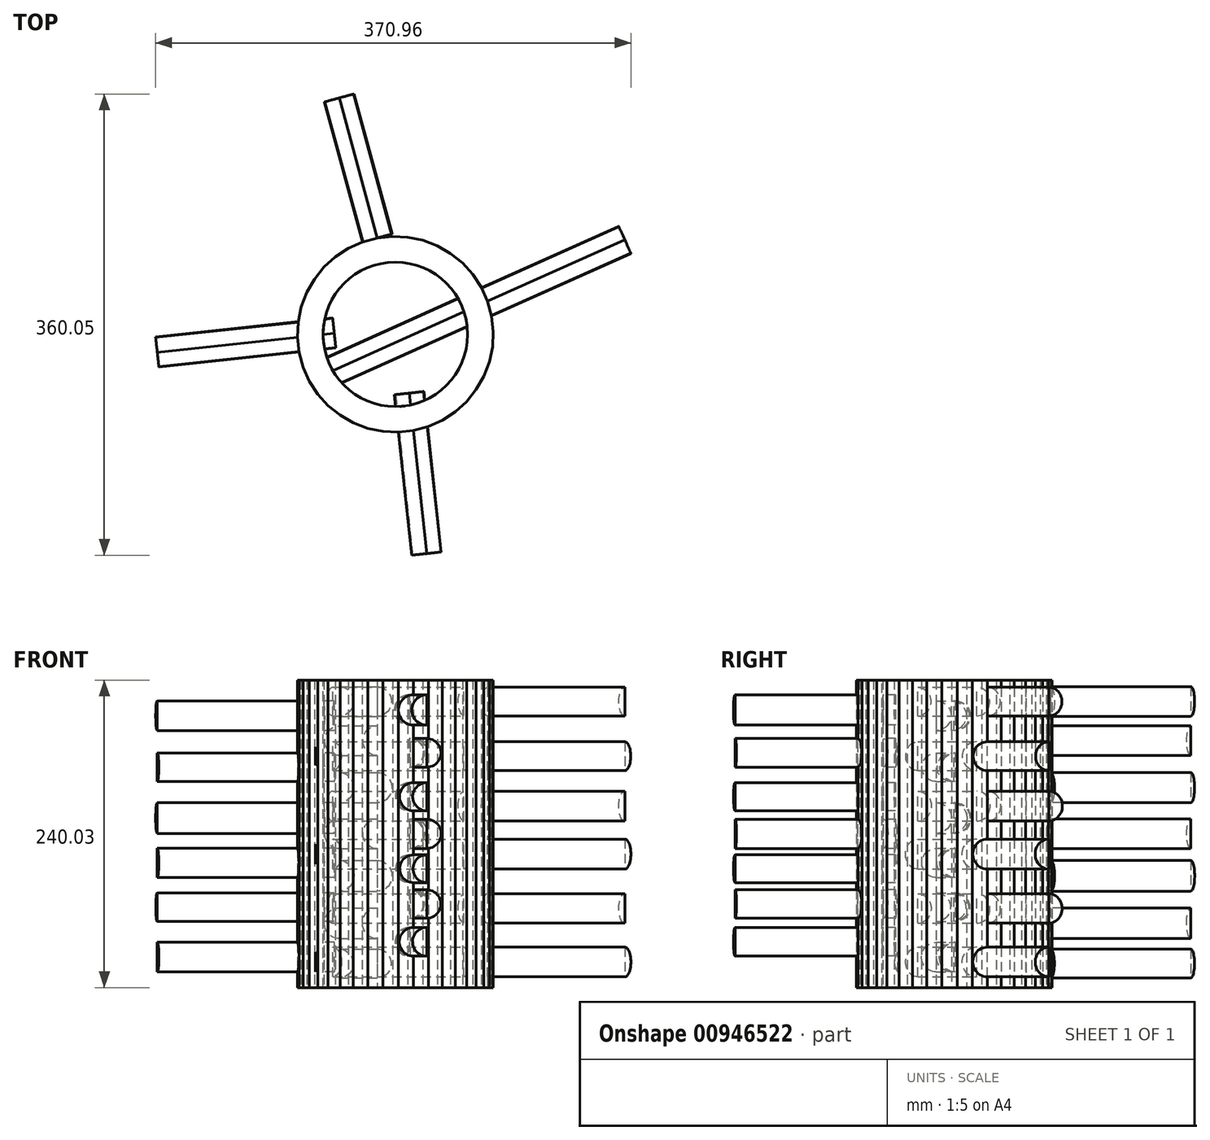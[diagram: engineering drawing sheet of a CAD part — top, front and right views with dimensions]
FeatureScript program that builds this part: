
annotation { "Feature Type Name" : "Feature", "Feature Type Description" : "" }
export const myFeature = defineFeature(function(context is Context, id is Id, definition is map)
    precondition{}
    {
        {
            var Q0;
            Q0=qCreatedBy(makeId("Top.planeOp"),FACE);
            var sketch = newSketch(context, id + "F0", { "sketchPlane" : qUnion([Q0])});
            skCircle(sketch, "E0.cCircle", {"center": v(0, 0) * mm, "radius": 76.25 * mm, "construction": true});
            skLineSegment(sketch, "E0.0", {"start": v(69.13, -32.73) * mm, "end": v(63.16, -43.14) * mm});
            skLineSegment(sketch, "E0.1", {"start": v(63.16, -43.14) * mm, "end": v(55.64, -52.5) * mm});
            skLineSegment(sketch, "E0.2", {"start": v(55.64, -52.5) * mm, "end": v(46.74, -60.55) * mm});
            skLineSegment(sketch, "E0.3", {"start": v(46.74, -60.55) * mm, "end": v(36.7, -67.11) * mm});
            skLineSegment(sketch, "E0.4", {"start": v(36.7, -67.11) * mm, "end": v(25.74, -72.03) * mm});
            skLineSegment(sketch, "E0.5", {"start": v(25.74, -72.03) * mm, "end": v(14.16, -75.17) * mm});
            skLineSegment(sketch, "E0.6", {"start": v(14.16, -75.17) * mm, "end": v(2.22, -76.46) * mm});
            skLineSegment(sketch, "E0.7", {"start": v(2.22, -76.46) * mm, "end": v(-9.76, -75.86) * mm});
            skLineSegment(sketch, "E0.8", {"start": v(-9.76, -75.86) * mm, "end": v(-21.51, -73.4) * mm});
            skLineSegment(sketch, "E0.9", {"start": v(-21.51, -73.4) * mm, "end": v(-32.73, -69.13) * mm});
            skLineSegment(sketch, "E0.10", {"start": v(-32.73, -69.13) * mm, "end": v(-43.14, -63.16) * mm});
            skLineSegment(sketch, "E0.11", {"start": v(-43.14, -63.16) * mm, "end": v(-52.5, -55.64) * mm});
            skLineSegment(sketch, "E0.12", {"start": v(-52.5, -55.64) * mm, "end": v(-60.55, -46.74) * mm});
            skLineSegment(sketch, "E0.13", {"start": v(-60.55, -46.74) * mm, "end": v(-67.11, -36.7) * mm});
            skLineSegment(sketch, "E0.14", {"start": v(-67.11, -36.7) * mm, "end": v(-72.03, -25.74) * mm});
            skLineSegment(sketch, "E0.15", {"start": v(-72.03, -25.74) * mm, "end": v(-75.17, -14.16) * mm});
            skLineSegment(sketch, "E0.16", {"start": v(-75.17, -14.16) * mm, "end": v(-76.46, -2.22) * mm});
            skLineSegment(sketch, "E0.17", {"start": v(-76.46, -2.22) * mm, "end": v(-75.86, 9.76) * mm});
            skLineSegment(sketch, "E0.18", {"start": v(-75.86, 9.76) * mm, "end": v(-73.4, 21.51) * mm});
            skLineSegment(sketch, "E0.19", {"start": v(-73.4, 21.51) * mm, "end": v(-69.13, 32.73) * mm});
            skLineSegment(sketch, "E0.20", {"start": v(-69.13, 32.73) * mm, "end": v(-63.16, 43.14) * mm});
            skLineSegment(sketch, "E0.21", {"start": v(-63.16, 43.14) * mm, "end": v(-55.64, 52.5) * mm});
            skLineSegment(sketch, "E0.22", {"start": v(-55.64, 52.5) * mm, "end": v(-46.74, 60.55) * mm});
            skLineSegment(sketch, "E0.23", {"start": v(-46.74, 60.55) * mm, "end": v(-36.7, 67.11) * mm});
            skLineSegment(sketch, "E0.24", {"start": v(-36.7, 67.11) * mm, "end": v(-25.74, 72.03) * mm});
            skLineSegment(sketch, "E0.25", {"start": v(-25.74, 72.03) * mm, "end": v(-14.16, 75.17) * mm});
            skLineSegment(sketch, "E0.26", {"start": v(-14.16, 75.17) * mm, "end": v(-2.22, 76.46) * mm});
            skLineSegment(sketch, "E0.27", {"start": v(-2.22, 76.46) * mm, "end": v(9.76, 75.86) * mm});
            skLineSegment(sketch, "E0.28", {"start": v(9.76, 75.86) * mm, "end": v(21.51, 73.4) * mm});
            skLineSegment(sketch, "E0.29", {"start": v(21.51, 73.4) * mm, "end": v(32.73, 69.13) * mm});
            skLineSegment(sketch, "E0.30", {"start": v(32.73, 69.13) * mm, "end": v(43.14, 63.16) * mm});
            skLineSegment(sketch, "E0.31", {"start": v(43.14, 63.16) * mm, "end": v(52.5, 55.64) * mm});
            skLineSegment(sketch, "E0.32", {"start": v(52.5, 55.64) * mm, "end": v(60.55, 46.74) * mm});
            skLineSegment(sketch, "E0.33", {"start": v(60.55, 46.74) * mm, "end": v(67.11, 36.7) * mm});
            skLineSegment(sketch, "E0.34", {"start": v(67.11, 36.7) * mm, "end": v(72.03, 25.74) * mm});
            skLineSegment(sketch, "E0.35", {"start": v(72.03, 25.74) * mm, "end": v(75.17, 14.16) * mm});
            skLineSegment(sketch, "E0.36", {"start": v(75.17, 14.16) * mm, "end": v(76.46, 2.22) * mm});
            skLineSegment(sketch, "E0.37", {"start": v(76.46, 2.22) * mm, "end": v(75.86, -9.76) * mm});
            skLineSegment(sketch, "E0.38", {"start": v(75.86, -9.76) * mm, "end": v(73.4, -21.51) * mm});
            skLineSegment(sketch, "E0.39", {"start": v(73.4, -21.51) * mm, "end": v(69.13, -32.73) * mm});
            skPoint(sketch, "E0.0.midPoint", {"position": v(66.15, -37.94) * mm});
            skSolve(sketch);
        }
        {
            var Q0;
            Q0=makeQuery(id+"F0.imprint","IMPRINT",FACE,{"disambiguationData":[TD([[makeQuery(id+"F0.imprint","IMPRINT",EDGE,{"derivedFrom":sQuery(id+"F0.wireOp",EDGE,"E0.0")}),-1.0]])]});
            extrude(context, id + "F1", {"entities" : qUnion([Q0]), "depth" : 240.03 * mm, "offsetDistance" : 25.4 * mm});
        }
        {
            var Q0;
            Q0=makeQuery(id+"F1.opExtrude","CAP_FACE",FACE,{"disambiguationData":[OSD([sQuery(id+"F0.wireOp",EDGE,"E0.0"),sQuery(id+"F0.wireOp",EDGE,"E0.1"),sQuery(id+"F0.wireOp",EDGE,"E0.2"),sQuery(id+"F0.wireOp",EDGE,"E0.3"),sQuery(id+"F0.wireOp",EDGE,"E0.4"),sQuery(id+"F0.wireOp",EDGE,"E0.5"),sQuery(id+"F0.wireOp",EDGE,"E0.6"),sQuery(id+"F0.wireOp",EDGE,"E0.7"),sQuery(id+"F0.wireOp",EDGE,"E0.8"),sQuery(id+"F0.wireOp",EDGE,"E0.9"),sQuery(id+"F0.wireOp",EDGE,"E0.10"),sQuery(id+"F0.wireOp",EDGE,"E0.11"),sQuery(id+"F0.wireOp",EDGE,"E0.12"),sQuery(id+"F0.wireOp",EDGE,"E0.13"),sQuery(id+"F0.wireOp",EDGE,"E0.14"),sQuery(id+"F0.wireOp",EDGE,"E0.15"),sQuery(id+"F0.wireOp",EDGE,"E0.16"),sQuery(id+"F0.wireOp",EDGE,"E0.17"),sQuery(id+"F0.wireOp",EDGE,"E0.18"),sQuery(id+"F0.wireOp",EDGE,"E0.19"),sQuery(id+"F0.wireOp",EDGE,"E0.20"),sQuery(id+"F0.wireOp",EDGE,"E0.21"),sQuery(id+"F0.wireOp",EDGE,"E0.22"),sQuery(id+"F0.wireOp",EDGE,"E0.23"),sQuery(id+"F0.wireOp",EDGE,"E0.24"),sQuery(id+"F0.wireOp",EDGE,"E0.25"),sQuery(id+"F0.wireOp",EDGE,"E0.26"),sQuery(id+"F0.wireOp",EDGE,"E0.27"),sQuery(id+"F0.wireOp",EDGE,"E0.28"),sQuery(id+"F0.wireOp",EDGE,"E0.29"),sQuery(id+"F0.wireOp",EDGE,"E0.30"),sQuery(id+"F0.wireOp",EDGE,"E0.31"),sQuery(id+"F0.wireOp",EDGE,"E0.32"),sQuery(id+"F0.wireOp",EDGE,"E0.33"),sQuery(id+"F0.wireOp",EDGE,"E0.34"),sQuery(id+"F0.wireOp",EDGE,"E0.35"),sQuery(id+"F0.wireOp",EDGE,"E0.36"),sQuery(id+"F0.wireOp",EDGE,"E0.37"),sQuery(id+"F0.wireOp",EDGE,"E0.38"),sQuery(id+"F0.wireOp",EDGE,"E0.39")])],"isStart":false});
            var sketch = newSketch(context, id + "F2", { "sketchPlane" : qUnion([Q0])});
            skCircle(sketch, "E1", {"center": v(0, 0) * mm, "radius": 56.38 * mm});
            skSolve(sketch);
        }
        {
            var Q0;
            Q0=makeQuery(id+"F2.imprint","IMPRINT",FACE,{"disambiguationData":[TD([[makeQuery(id+"F2.imprint","IMPRINT",EDGE,{"derivedFrom":sQuery(id+"F2.wireOp",EDGE,"E1")}),1.0]])]});
            extrude(context, id + "F3", {"entities" : qUnion([Q0]), "operationType" : NewBodyOperationType.REMOVE, "oppositeDirection" : true, "depth" : 425.96 * mm, "offsetDistance" : 25.4 * mm});
        }
        {
            var Q0;
            Q0=makeQuery(id+"F1.opExtrude","SWEPT_FACE",FACE,{"disambiguationData":[OSD([sQuery(id+"F0.wireOp",EDGE,"E0.6")])]});
            var sketch = newSketch(context, id + "F4", { "sketchPlane" : qUnion([Q0])});
            skCircle(sketch, "E2", {"center": v(6, 183.22) * mm, "radius": 11.15 * mm});
            skCircle(sketch, "E3", {"center": v(6, 149) * mm, "radius": 11.02 * mm});
            skPoint(sketch, "E4.center.orphan", {"position": v(6, 120.02) * mm});
            skCircle(sketch, "E5", {"center": v(6, 120.02) * mm, "radius": 11.4 * mm});
            skCircle(sketch, "E6", {"center": v(6, 92.73) * mm, "radius": 10.84 * mm});
            skCircle(sketch, "E7", {"center": v(6, 65.2) * mm, "radius": 11.04 * mm});
            skCircle(sketch, "E8", {"center": v(6, 35.69) * mm, "radius": 11.2 * mm});
            skCircle(sketch, "E9", {"center": v(6, 216.66) * mm, "radius": 11.8 * mm});
            skSolve(sketch);
        }
        {
            var Q0;
            {var subQ0=sQuery(id+"F4.wireOp",EDGE,"E9");var subQ1=makeQuery(id+"F1.opExtrude","SWEPT_EDGE",EDGE,{"disambiguationData":[OSD([sQuery(id+"F0.wireOp",EDGE,"E0.5"),sQuery(id+"F0.wireOp",EDGE,"E0.6")])]});var subQ2=makeQuery(id+"F4.imprint","INTERSECT",VERTEX,{"disambiguationData":[OD(0.0)],"derivedFrom":[subQ1,subQ0]});Q0=makeQuery(id+"F4.imprint","IMPRINT",FACE,{"disambiguationData":[TD([[makeQuery(id+"F4.imprint","IMPRINT",EDGE,{"disambiguationData":[TD([[subQ2,-1.0]])],"derivedFrom":subQ0}),1.0]])]});}
            var Q1;
            {var subQ0=sQuery(id+"F4.wireOp",EDGE,"E2");var subQ1=makeQuery(id+"F1.opExtrude","SWEPT_EDGE",EDGE,{"disambiguationData":[OSD([sQuery(id+"F0.wireOp",EDGE,"E0.5"),sQuery(id+"F0.wireOp",EDGE,"E0.6")])]});var subQ2=makeQuery(id+"F4.imprint","INTERSECT",VERTEX,{"disambiguationData":[OD(0.0)],"derivedFrom":[subQ1,subQ0]});Q1=makeQuery(id+"F4.imprint","IMPRINT",FACE,{"disambiguationData":[TD([[makeQuery(id+"F4.imprint","IMPRINT",EDGE,{"disambiguationData":[TD([[subQ2,1.0]])],"derivedFrom":subQ0}),1.0]])]});}
            var Q2;
            {var subQ0=sQuery(id+"F4.wireOp",EDGE,"E3");var subQ1=makeQuery(id+"F1.opExtrude","SWEPT_EDGE",EDGE,{"disambiguationData":[OSD([sQuery(id+"F0.wireOp",EDGE,"E0.5"),sQuery(id+"F0.wireOp",EDGE,"E0.6")])]});var subQ2=makeQuery(id+"F4.imprint","INTERSECT",VERTEX,{"disambiguationData":[OD(0.0)],"derivedFrom":[subQ1,subQ0]});Q2=makeQuery(id+"F4.imprint","IMPRINT",FACE,{"disambiguationData":[TD([[makeQuery(id+"F4.imprint","IMPRINT",EDGE,{"disambiguationData":[TD([[subQ2,-1.0]])],"derivedFrom":subQ0}),1.0]])]});}
            var Q3;
            {var subQ0=sQuery(id+"F4.wireOp",EDGE,"E5");var subQ1=makeQuery(id+"F1.opExtrude","SWEPT_EDGE",EDGE,{"disambiguationData":[OSD([sQuery(id+"F0.wireOp",EDGE,"E0.5"),sQuery(id+"F0.wireOp",EDGE,"E0.6")])]});var subQ2=makeQuery(id+"F4.imprint","INTERSECT",VERTEX,{"disambiguationData":[OD(0.0)],"derivedFrom":[subQ1,subQ0]});Q3=makeQuery(id+"F4.imprint","IMPRINT",FACE,{"disambiguationData":[TD([[makeQuery(id+"F4.imprint","IMPRINT",EDGE,{"disambiguationData":[TD([[subQ2,1.0]])],"derivedFrom":subQ0}),1.0]])]});}
            var Q4;
            {var subQ0=sQuery(id+"F4.wireOp",EDGE,"E6");var subQ1=makeQuery(id+"F1.opExtrude","SWEPT_EDGE",EDGE,{"disambiguationData":[OSD([sQuery(id+"F0.wireOp",EDGE,"E0.5"),sQuery(id+"F0.wireOp",EDGE,"E0.6")])]});var subQ2=makeQuery(id+"F4.imprint","INTERSECT",VERTEX,{"disambiguationData":[OD(0.0)],"derivedFrom":[subQ1,subQ0]});Q4=makeQuery(id+"F4.imprint","IMPRINT",FACE,{"disambiguationData":[TD([[makeQuery(id+"F4.imprint","IMPRINT",EDGE,{"disambiguationData":[TD([[subQ2,1.0]])],"derivedFrom":subQ0}),1.0]])]});}
            var Q5;
            {var subQ0=sQuery(id+"F4.wireOp",EDGE,"E7");var subQ1=makeQuery(id+"F1.opExtrude","SWEPT_EDGE",EDGE,{"disambiguationData":[OSD([sQuery(id+"F0.wireOp",EDGE,"E0.5"),sQuery(id+"F0.wireOp",EDGE,"E0.6")])]});var subQ2=makeQuery(id+"F4.imprint","INTERSECT",VERTEX,{"disambiguationData":[OD(0.0)],"derivedFrom":[subQ1,subQ0]});Q5=makeQuery(id+"F4.imprint","IMPRINT",FACE,{"disambiguationData":[TD([[makeQuery(id+"F4.imprint","IMPRINT",EDGE,{"disambiguationData":[TD([[subQ2,-1.0]])],"derivedFrom":subQ0}),1.0]])]});}
            var Q6;
            {var subQ0=sQuery(id+"F4.wireOp",EDGE,"E8");var subQ1=makeQuery(id+"F1.opExtrude","SWEPT_EDGE",EDGE,{"disambiguationData":[OSD([sQuery(id+"F0.wireOp",EDGE,"E0.5"),sQuery(id+"F0.wireOp",EDGE,"E0.6")])]});var subQ2=makeQuery(id+"F4.imprint","INTERSECT",VERTEX,{"disambiguationData":[OD(0.0)],"derivedFrom":[subQ1,subQ0]});Q6=makeQuery(id+"F4.imprint","IMPRINT",FACE,{"disambiguationData":[TD([[makeQuery(id+"F4.imprint","IMPRINT",EDGE,{"disambiguationData":[TD([[subQ2,1.0]])],"derivedFrom":subQ0}),1.0]])]});}
            extrude(context, id + "F5", {"entities" : qUnion([Q0, Q1, Q2, Q3, Q4, Q5, Q6]), "operationType" : NewBodyOperationType.ADD, "oppositeDirection" : true, "depth" : 29.46 * mm, "offsetDistance" : 25.4 * mm});
        }
        {
            var Q0;
            Q0=makeQuery(id+"F5.opExtrude","CAP_FACE",FACE,{"disambiguationData":[OSD([sQuery(id+"F0.wireOp",EDGE,"E0.5"),sQuery(id+"F0.wireOp",EDGE,"E0.6"),sQuery(id+"F4.wireOp",EDGE,"E9")])],"isStart":false});
            var Q1;
            Q1=makeQuery(id+"F5.opExtrude","CAP_FACE",FACE,{"disambiguationData":[OSD([sQuery(id+"F0.wireOp",EDGE,"E0.5"),sQuery(id+"F0.wireOp",EDGE,"E0.6"),sQuery(id+"F4.wireOp",EDGE,"E2")])],"isStart":false});
            var Q2;
            Q2=makeQuery(id+"F5.opExtrude","CAP_FACE",FACE,{"disambiguationData":[OSD([sQuery(id+"F0.wireOp",EDGE,"E0.5"),sQuery(id+"F0.wireOp",EDGE,"E0.6"),sQuery(id+"F4.wireOp",EDGE,"E3")])],"isStart":false});
            var Q3;
            Q3=makeQuery(id+"F5.opExtrude","CAP_FACE",FACE,{"disambiguationData":[OSD([sQuery(id+"F0.wireOp",EDGE,"E0.5"),sQuery(id+"F0.wireOp",EDGE,"E0.6"),sQuery(id+"F4.wireOp",EDGE,"E5")])],"isStart":false});
            var Q4;
            Q4=makeQuery(id+"F5.opExtrude","CAP_FACE",FACE,{"disambiguationData":[OSD([sQuery(id+"F0.wireOp",EDGE,"E0.5"),sQuery(id+"F0.wireOp",EDGE,"E0.6"),sQuery(id+"F4.wireOp",EDGE,"E6")])],"isStart":false});
            var Q5;
            Q5=makeQuery(id+"F5.opExtrude","CAP_FACE",FACE,{"disambiguationData":[OSD([sQuery(id+"F0.wireOp",EDGE,"E0.5"),sQuery(id+"F0.wireOp",EDGE,"E0.6"),sQuery(id+"F4.wireOp",EDGE,"E8")])],"isStart":false});
            var Q6;
            Q6=makeQuery(id+"F5.opExtrude","CAP_FACE",FACE,{"disambiguationData":[OSD([sQuery(id+"F0.wireOp",EDGE,"E0.5"),sQuery(id+"F0.wireOp",EDGE,"E0.6"),sQuery(id+"F4.wireOp",EDGE,"E7")])],"isStart":false});
            extrude(context, id + "F6", {"entities" : qUnion([Q0, Q1, Q2, Q3, Q4, Q5, Q6]), "operationType" : NewBodyOperationType.ADD, "oppositeDirection" : true, "depth" : 125.98 * mm, "offsetDistance" : 25.4 * mm});
        }
        {
            var Q0;
            Q0=makeQuery(id+"F1.opExtrude","SWEPT_FACE",FACE,{"disambiguationData":[OSD([sQuery(id+"F0.wireOp",EDGE,"E0.25")])]});
            var sketch = newSketch(context, id + "F7", { "sketchPlane" : qUnion([Q0])});
            skCircle(sketch, "E10", {"center": v(-6, 223.35) * mm, "radius": 11.6 * mm});
            skCircle(sketch, "E11", {"center": v(-6, 192.66) * mm, "radius": 11.6 * mm});
            skCircle(sketch, "E12", {"center": v(-6, 156.07) * mm, "radius": 11.78 * mm});
            skCircle(sketch, "E13", {"center": v(-6, 120.02) * mm, "radius": 11.63 * mm});
            skCircle(sketch, "E14", {"center": v(-6, 87.23) * mm, "radius": 12.03 * mm});
            skCircle(sketch, "E15", {"center": v(-6, 50.25) * mm, "radius": 11.97 * mm});
            skCircle(sketch, "E16", {"center": v(-6, 18.77) * mm, "radius": 11.25 * mm});
            skSolve(sketch);
        }
        {
            var Q0;
            {var subQ0=sQuery(id+"F7.wireOp",EDGE,"E10");var subQ1=makeQuery(id+"F1.opExtrude","SWEPT_EDGE",EDGE,{"disambiguationData":[OSD([sQuery(id+"F0.wireOp",EDGE,"E0.25"),sQuery(id+"F0.wireOp",EDGE,"E0.26")])]});var subQ2=makeQuery(id+"F7.imprint","INTERSECT",VERTEX,{"disambiguationData":[OD(0.0)],"derivedFrom":[subQ1,subQ0]});Q0=makeQuery(id+"F7.imprint","IMPRINT",FACE,{"disambiguationData":[TD([[makeQuery(id+"F7.imprint","IMPRINT",EDGE,{"disambiguationData":[TD([[subQ2,-1.0]])],"derivedFrom":subQ0}),1.0]])]});}
            var Q1;
            {var subQ0=sQuery(id+"F7.wireOp",EDGE,"E11");var subQ1=makeQuery(id+"F1.opExtrude","SWEPT_EDGE",EDGE,{"disambiguationData":[OSD([sQuery(id+"F0.wireOp",EDGE,"E0.25"),sQuery(id+"F0.wireOp",EDGE,"E0.26")])]});var subQ2=makeQuery(id+"F7.imprint","INTERSECT",VERTEX,{"disambiguationData":[OD(0.0)],"derivedFrom":[subQ1,subQ0]});Q1=makeQuery(id+"F7.imprint","IMPRINT",FACE,{"disambiguationData":[TD([[makeQuery(id+"F7.imprint","IMPRINT",EDGE,{"disambiguationData":[TD([[subQ2,1.0]])],"derivedFrom":subQ0}),1.0]])]});}
            var Q2;
            {var subQ0=sQuery(id+"F7.wireOp",EDGE,"E12");var subQ1=makeQuery(id+"F1.opExtrude","SWEPT_EDGE",EDGE,{"disambiguationData":[OSD([sQuery(id+"F0.wireOp",EDGE,"E0.25"),sQuery(id+"F0.wireOp",EDGE,"E0.26")])]});var subQ2=makeQuery(id+"F7.imprint","INTERSECT",VERTEX,{"disambiguationData":[OD(0.0)],"derivedFrom":[subQ1,subQ0]});Q2=makeQuery(id+"F7.imprint","IMPRINT",FACE,{"disambiguationData":[TD([[makeQuery(id+"F7.imprint","IMPRINT",EDGE,{"disambiguationData":[TD([[subQ2,1.0]])],"derivedFrom":subQ0}),1.0]])]});}
            var Q3;
            {var subQ0=sQuery(id+"F7.wireOp",EDGE,"E13");var subQ1=makeQuery(id+"F1.opExtrude","SWEPT_EDGE",EDGE,{"disambiguationData":[OSD([sQuery(id+"F0.wireOp",EDGE,"E0.25"),sQuery(id+"F0.wireOp",EDGE,"E0.26")])]});var subQ2=makeQuery(id+"F7.imprint","INTERSECT",VERTEX,{"disambiguationData":[OD(0.0)],"derivedFrom":[subQ1,subQ0]});Q3=makeQuery(id+"F7.imprint","IMPRINT",FACE,{"disambiguationData":[TD([[makeQuery(id+"F7.imprint","IMPRINT",EDGE,{"disambiguationData":[TD([[subQ2,-1.0]])],"derivedFrom":subQ0}),1.0]])]});}
            var Q4;
            {var subQ0=sQuery(id+"F7.wireOp",EDGE,"E14");var subQ1=makeQuery(id+"F1.opExtrude","SWEPT_EDGE",EDGE,{"disambiguationData":[OSD([sQuery(id+"F0.wireOp",EDGE,"E0.25"),sQuery(id+"F0.wireOp",EDGE,"E0.26")])]});var subQ2=makeQuery(id+"F7.imprint","INTERSECT",VERTEX,{"disambiguationData":[OD(0.0)],"derivedFrom":[subQ1,subQ0]});Q4=makeQuery(id+"F7.imprint","IMPRINT",FACE,{"disambiguationData":[TD([[makeQuery(id+"F7.imprint","IMPRINT",EDGE,{"disambiguationData":[TD([[subQ2,-1.0]])],"derivedFrom":subQ0}),1.0]])]});}
            var Q5;
            {var subQ0=sQuery(id+"F7.wireOp",EDGE,"E15");var subQ1=makeQuery(id+"F1.opExtrude","SWEPT_EDGE",EDGE,{"disambiguationData":[OSD([sQuery(id+"F0.wireOp",EDGE,"E0.25"),sQuery(id+"F0.wireOp",EDGE,"E0.26")])]});var subQ2=makeQuery(id+"F7.imprint","INTERSECT",VERTEX,{"disambiguationData":[OD(0.0)],"derivedFrom":[subQ1,subQ0]});Q5=makeQuery(id+"F7.imprint","IMPRINT",FACE,{"disambiguationData":[TD([[makeQuery(id+"F7.imprint","IMPRINT",EDGE,{"disambiguationData":[TD([[subQ2,1.0]])],"derivedFrom":subQ0}),1.0]])]});}
            var Q6;
            {var subQ0=sQuery(id+"F7.wireOp",EDGE,"E16");var subQ1=makeQuery(id+"F1.opExtrude","SWEPT_EDGE",EDGE,{"disambiguationData":[OSD([sQuery(id+"F0.wireOp",EDGE,"E0.25"),sQuery(id+"F0.wireOp",EDGE,"E0.26")])]});var subQ2=makeQuery(id+"F7.imprint","INTERSECT",VERTEX,{"disambiguationData":[OD(0.0)],"derivedFrom":[subQ1,subQ0]});Q6=makeQuery(id+"F7.imprint","IMPRINT",FACE,{"disambiguationData":[TD([[makeQuery(id+"F7.imprint","IMPRINT",EDGE,{"disambiguationData":[TD([[subQ2,1.0]])],"derivedFrom":subQ0}),1.0]])]});}
            extrude(context, id + "F8", {"entities" : qUnion([Q0, Q1, Q2, Q3, Q4, Q5, Q6]), "operationType" : NewBodyOperationType.ADD, "depth" : 113.28 * mm, "offsetDistance" : 25.4 * mm});
        }
        {
            var Q0;
            Q0=makeQuery(id+"F1.opExtrude","SWEPT_FACE",FACE,{"disambiguationData":[OSD([sQuery(id+"F0.wireOp",EDGE,"E0.16")])]});
            var sketch = newSketch(context, id + "F9", { "sketchPlane" : qUnion([Q0])});
            skCircle(sketch, "E17", {"center": v(-6, 23.76) * mm, "radius": 11.6 * mm});
            skCircle(sketch, "E18", {"center": v(-6, 62.71) * mm, "radius": 11.2 * mm});
            skCircle(sketch, "E19", {"center": v(-6, 97.29) * mm, "radius": 11.37 * mm});
            skCircle(sketch, "E20", {"center": v(-6, 132.3) * mm, "radius": 11.97 * mm});
            skCircle(sketch, "E21", {"center": v(-6, 171.94) * mm, "radius": 11.22 * mm});
            skCircle(sketch, "E22", {"center": v(-6, 212.2) * mm, "radius": 11.6 * mm});
            skSolve(sketch);
        }
        {
            var Q0;
            {var subQ0=sQuery(id+"F9.wireOp",EDGE,"E17");var subQ1=makeQuery(id+"F1.opExtrude","SWEPT_EDGE",EDGE,{"disambiguationData":[OSD([sQuery(id+"F0.wireOp",EDGE,"E0.16"),sQuery(id+"F0.wireOp",EDGE,"E0.17")])]});var subQ2=makeQuery(id+"F9.imprint","INTERSECT",VERTEX,{"disambiguationData":[OD(0.0)],"derivedFrom":[subQ1,subQ0]});Q0=makeQuery(id+"F9.imprint","IMPRINT",FACE,{"disambiguationData":[TD([[makeQuery(id+"F9.imprint","IMPRINT",EDGE,{"disambiguationData":[TD([[subQ2,-1.0]])],"derivedFrom":subQ0}),1.0]])]});}
            var Q1;
            {var subQ0=sQuery(id+"F9.wireOp",EDGE,"E18");var subQ1=makeQuery(id+"F1.opExtrude","SWEPT_EDGE",EDGE,{"disambiguationData":[OSD([sQuery(id+"F0.wireOp",EDGE,"E0.16"),sQuery(id+"F0.wireOp",EDGE,"E0.17")])]});var subQ2=makeQuery(id+"F9.imprint","INTERSECT",VERTEX,{"disambiguationData":[OD(0.0)],"derivedFrom":[subQ1,subQ0]});Q1=makeQuery(id+"F9.imprint","IMPRINT",FACE,{"disambiguationData":[TD([[makeQuery(id+"F9.imprint","IMPRINT",EDGE,{"disambiguationData":[TD([[subQ2,1.0]])],"derivedFrom":subQ0}),1.0]])]});}
            var Q2;
            {var subQ0=sQuery(id+"F9.wireOp",EDGE,"E19");var subQ1=makeQuery(id+"F1.opExtrude","SWEPT_EDGE",EDGE,{"disambiguationData":[OSD([sQuery(id+"F0.wireOp",EDGE,"E0.16"),sQuery(id+"F0.wireOp",EDGE,"E0.17")])]});var subQ2=makeQuery(id+"F9.imprint","INTERSECT",VERTEX,{"disambiguationData":[OD(0.0)],"derivedFrom":[subQ1,subQ0]});Q2=makeQuery(id+"F9.imprint","IMPRINT",FACE,{"disambiguationData":[TD([[makeQuery(id+"F9.imprint","IMPRINT",EDGE,{"disambiguationData":[TD([[subQ2,-1.0]])],"derivedFrom":subQ0}),1.0]])]});}
            var Q3;
            {var subQ0=sQuery(id+"F9.wireOp",EDGE,"E20");var subQ1=makeQuery(id+"F1.opExtrude","SWEPT_EDGE",EDGE,{"disambiguationData":[OSD([sQuery(id+"F0.wireOp",EDGE,"E0.16"),sQuery(id+"F0.wireOp",EDGE,"E0.17")])]});var subQ2=makeQuery(id+"F9.imprint","INTERSECT",VERTEX,{"disambiguationData":[OD(0.0)],"derivedFrom":[subQ1,subQ0]});Q3=makeQuery(id+"F9.imprint","IMPRINT",FACE,{"disambiguationData":[TD([[makeQuery(id+"F9.imprint","IMPRINT",EDGE,{"disambiguationData":[TD([[subQ2,-1.0]])],"derivedFrom":subQ0}),1.0]])]});}
            var Q4;
            {var subQ0=sQuery(id+"F9.wireOp",EDGE,"E21");var subQ1=makeQuery(id+"F1.opExtrude","SWEPT_EDGE",EDGE,{"disambiguationData":[OSD([sQuery(id+"F0.wireOp",EDGE,"E0.16"),sQuery(id+"F0.wireOp",EDGE,"E0.17")])]});var subQ2=makeQuery(id+"F9.imprint","INTERSECT",VERTEX,{"disambiguationData":[OD(0.0)],"derivedFrom":[subQ1,subQ0]});Q4=makeQuery(id+"F9.imprint","IMPRINT",FACE,{"disambiguationData":[TD([[makeQuery(id+"F9.imprint","IMPRINT",EDGE,{"disambiguationData":[TD([[subQ2,1.0]])],"derivedFrom":subQ0}),1.0]])]});}
            var Q5;
            {var subQ0=sQuery(id+"F9.wireOp",EDGE,"E22");var subQ1=makeQuery(id+"F1.opExtrude","SWEPT_EDGE",EDGE,{"disambiguationData":[OSD([sQuery(id+"F0.wireOp",EDGE,"E0.16"),sQuery(id+"F0.wireOp",EDGE,"E0.17")])]});var subQ2=makeQuery(id+"F9.imprint","INTERSECT",VERTEX,{"disambiguationData":[OD(0.0)],"derivedFrom":[subQ1,subQ0]});Q5=makeQuery(id+"F9.imprint","IMPRINT",FACE,{"disambiguationData":[TD([[makeQuery(id+"F9.imprint","IMPRINT",EDGE,{"disambiguationData":[TD([[subQ2,-1.0]])],"derivedFrom":subQ0}),1.0]])]});}
            extrude(context, id + "F10", {"entities" : qUnion([Q0, Q1, Q2, Q3, Q4, Q5]), "operationType" : NewBodyOperationType.ADD, "oppositeDirection" : true, "depth" : 28.96 * mm, "offsetDistance" : 25.4 * mm});
        }
        {
            var Q0;
            Q0=makeQuery(id+"F10.opExtrude","CAP_FACE",FACE,{"disambiguationData":[OSD([sQuery(id+"F0.wireOp",EDGE,"E0.16"),sQuery(id+"F0.wireOp",EDGE,"E0.17"),sQuery(id+"F9.wireOp",EDGE,"E17")])],"isStart":false});
            var Q1;
            Q1=makeQuery(id+"F10.opExtrude","CAP_FACE",FACE,{"disambiguationData":[OSD([sQuery(id+"F0.wireOp",EDGE,"E0.16"),sQuery(id+"F0.wireOp",EDGE,"E0.17"),sQuery(id+"F9.wireOp",EDGE,"E18")])],"isStart":false});
            var Q2;
            Q2=makeQuery(id+"F10.opExtrude","CAP_FACE",FACE,{"disambiguationData":[OSD([sQuery(id+"F0.wireOp",EDGE,"E0.16"),sQuery(id+"F0.wireOp",EDGE,"E0.17"),sQuery(id+"F9.wireOp",EDGE,"E19")])],"isStart":false});
            var Q3;
            Q3=makeQuery(id+"F10.opExtrude","CAP_FACE",FACE,{"disambiguationData":[OSD([sQuery(id+"F0.wireOp",EDGE,"E0.16"),sQuery(id+"F0.wireOp",EDGE,"E0.17"),sQuery(id+"F9.wireOp",EDGE,"E20")])],"isStart":false});
            var Q4;
            Q4=makeQuery(id+"F10.opExtrude","CAP_FACE",FACE,{"disambiguationData":[OSD([sQuery(id+"F0.wireOp",EDGE,"E0.16"),sQuery(id+"F0.wireOp",EDGE,"E0.17"),sQuery(id+"F9.wireOp",EDGE,"E21")])],"isStart":false});
            var Q5;
            Q5=makeQuery(id+"F10.opExtrude","CAP_FACE",FACE,{"disambiguationData":[OSD([sQuery(id+"F0.wireOp",EDGE,"E0.16"),sQuery(id+"F0.wireOp",EDGE,"E0.17"),sQuery(id+"F9.wireOp",EDGE,"E22")])],"isStart":false});
            extrude(context, id + "F11", {"entities" : qUnion([Q0, Q1, Q2, Q3, Q4, Q5]), "operationType" : NewBodyOperationType.ADD, "oppositeDirection" : true, "depth" : 138.94 * mm, "offsetDistance" : 25.4 * mm});
        }
        {
            var Q0;
            Q0=makeQuery(id+"F1.opExtrude","SWEPT_FACE",FACE,{"disambiguationData":[OSD([sQuery(id+"F0.wireOp",EDGE,"E0.34")])]});
            var sketch = newSketch(context, id + "F12", { "sketchPlane" : qUnion([Q0])});
            skCircle(sketch, "E23", {"center": v(-6, 223.24) * mm, "radius": 11.2 * mm});
            skCircle(sketch, "E24", {"center": v(-6, 180.61) * mm, "radius": 11.28 * mm});
            skCircle(sketch, "E25", {"center": v(-6, 141.72) * mm, "radius": 11.63 * mm});
            skCircle(sketch, "E26", {"center": v(-6, 104.21) * mm, "radius": 11.67 * mm});
            skCircle(sketch, "E27", {"center": v(-6, 61.77) * mm, "radius": 11.41 * mm});
            skCircle(sketch, "E28", {"center": v(-6, 19.96) * mm, "radius": 11.57 * mm});
            skSolve(sketch);
        }
        {
            var Q0;
            {var subQ0=sQuery(id+"F12.wireOp",EDGE,"E23");var subQ1=makeQuery(id+"F1.opExtrude","SWEPT_EDGE",EDGE,{"disambiguationData":[OSD([sQuery(id+"F0.wireOp",EDGE,"E0.34"),sQuery(id+"F0.wireOp",EDGE,"E0.35")])]});var subQ2=makeQuery(id+"F12.imprint","INTERSECT",VERTEX,{"disambiguationData":[OD(0.0)],"derivedFrom":[subQ1,subQ0]});Q0=makeQuery(id+"F12.imprint","IMPRINT",FACE,{"disambiguationData":[TD([[makeQuery(id+"F12.imprint","IMPRINT",EDGE,{"disambiguationData":[TD([[subQ2,1.0]])],"derivedFrom":subQ0}),1.0]])]});}
            var Q1;
            {var subQ0=sQuery(id+"F12.wireOp",EDGE,"E24");var subQ1=makeQuery(id+"F1.opExtrude","SWEPT_EDGE",EDGE,{"disambiguationData":[OSD([sQuery(id+"F0.wireOp",EDGE,"E0.34"),sQuery(id+"F0.wireOp",EDGE,"E0.35")])]});var subQ2=makeQuery(id+"F12.imprint","INTERSECT",VERTEX,{"disambiguationData":[OD(0.0)],"derivedFrom":[subQ1,subQ0]});Q1=makeQuery(id+"F12.imprint","IMPRINT",FACE,{"disambiguationData":[TD([[makeQuery(id+"F12.imprint","IMPRINT",EDGE,{"disambiguationData":[TD([[subQ2,-1.0]])],"derivedFrom":subQ0}),1.0]])]});}
            var Q2;
            {var subQ0=sQuery(id+"F12.wireOp",EDGE,"E25");var subQ1=makeQuery(id+"F1.opExtrude","SWEPT_EDGE",EDGE,{"disambiguationData":[OSD([sQuery(id+"F0.wireOp",EDGE,"E0.34"),sQuery(id+"F0.wireOp",EDGE,"E0.35")])]});var subQ2=makeQuery(id+"F12.imprint","INTERSECT",VERTEX,{"disambiguationData":[OD(0.0)],"derivedFrom":[subQ1,subQ0]});Q2=makeQuery(id+"F12.imprint","IMPRINT",FACE,{"disambiguationData":[TD([[makeQuery(id+"F12.imprint","IMPRINT",EDGE,{"disambiguationData":[TD([[subQ2,1.0]])],"derivedFrom":subQ0}),1.0]])]});}
            var Q3;
            {var subQ0=sQuery(id+"F12.wireOp",EDGE,"E26");var subQ1=makeQuery(id+"F1.opExtrude","SWEPT_EDGE",EDGE,{"disambiguationData":[OSD([sQuery(id+"F0.wireOp",EDGE,"E0.34"),sQuery(id+"F0.wireOp",EDGE,"E0.35")])]});var subQ2=makeQuery(id+"F12.imprint","INTERSECT",VERTEX,{"disambiguationData":[OD(0.0)],"derivedFrom":[subQ1,subQ0]});Q3=makeQuery(id+"F12.imprint","IMPRINT",FACE,{"disambiguationData":[TD([[makeQuery(id+"F12.imprint","IMPRINT",EDGE,{"disambiguationData":[TD([[subQ2,1.0]])],"derivedFrom":subQ0}),1.0]])]});}
            var Q4;
            {var subQ0=sQuery(id+"F12.wireOp",EDGE,"E27");var subQ1=makeQuery(id+"F1.opExtrude","SWEPT_EDGE",EDGE,{"disambiguationData":[OSD([sQuery(id+"F0.wireOp",EDGE,"E0.34"),sQuery(id+"F0.wireOp",EDGE,"E0.35")])]});var subQ2=makeQuery(id+"F12.imprint","INTERSECT",VERTEX,{"disambiguationData":[OD(0.0)],"derivedFrom":[subQ1,subQ0]});Q4=makeQuery(id+"F12.imprint","IMPRINT",FACE,{"disambiguationData":[TD([[makeQuery(id+"F12.imprint","IMPRINT",EDGE,{"disambiguationData":[TD([[subQ2,-1.0]])],"derivedFrom":subQ0}),1.0]])]});}
            var Q5;
            {var subQ0=sQuery(id+"F12.wireOp",EDGE,"E28");var subQ1=makeQuery(id+"F1.opExtrude","SWEPT_EDGE",EDGE,{"disambiguationData":[OSD([sQuery(id+"F0.wireOp",EDGE,"E0.34"),sQuery(id+"F0.wireOp",EDGE,"E0.35")])]});var subQ2=makeQuery(id+"F12.imprint","INTERSECT",VERTEX,{"disambiguationData":[OD(0.0)],"derivedFrom":[subQ1,subQ0]});Q5=makeQuery(id+"F12.imprint","IMPRINT",FACE,{"disambiguationData":[TD([[makeQuery(id+"F12.imprint","IMPRINT",EDGE,{"disambiguationData":[TD([[subQ2,1.0]])],"derivedFrom":subQ0}),1.0]])]});}
            extrude(context, id + "F13", {"entities" : qUnion([Q0, Q1, Q2, Q3, Q4, Q5]), "operationType" : NewBodyOperationType.ADD, "oppositeDirection" : true, "depth" : 30.73 * mm, "offsetDistance" : 25.4 * mm});
        }
        {
            var Q0;
            Q0=makeQuery(id+"F13.opExtrude","CAP_FACE",FACE,{"disambiguationData":[OSD([sQuery(id+"F0.wireOp",EDGE,"E0.34"),sQuery(id+"F0.wireOp",EDGE,"E0.35"),sQuery(id+"F12.wireOp",EDGE,"E23")])],"isStart":false});
            var Q1;
            Q1=makeQuery(id+"F13.opExtrude","CAP_FACE",FACE,{"disambiguationData":[OSD([sQuery(id+"F0.wireOp",EDGE,"E0.34"),sQuery(id+"F0.wireOp",EDGE,"E0.35"),sQuery(id+"F12.wireOp",EDGE,"E25")])],"isStart":false});
            var Q2;
            Q2=makeQuery(id+"F13.opExtrude","CAP_FACE",FACE,{"disambiguationData":[OSD([sQuery(id+"F0.wireOp",EDGE,"E0.34"),sQuery(id+"F0.wireOp",EDGE,"E0.35"),sQuery(id+"F12.wireOp",EDGE,"E26")])],"isStart":false});
            var Q3;
            Q3=makeQuery(id+"F13.opExtrude","CAP_FACE",FACE,{"disambiguationData":[OSD([sQuery(id+"F0.wireOp",EDGE,"E0.34"),sQuery(id+"F0.wireOp",EDGE,"E0.35"),sQuery(id+"F12.wireOp",EDGE,"E24")])],"isStart":false});
            var Q4;
            Q4=makeQuery(id+"F13.opExtrude","CAP_FACE",FACE,{"disambiguationData":[OSD([sQuery(id+"F0.wireOp",EDGE,"E0.34"),sQuery(id+"F0.wireOp",EDGE,"E0.35"),sQuery(id+"F12.wireOp",EDGE,"E27")])],"isStart":false});
            var Q5;
            Q5=makeQuery(id+"F13.opExtrude","CAP_FACE",FACE,{"disambiguationData":[OSD([sQuery(id+"F0.wireOp",EDGE,"E0.34"),sQuery(id+"F0.wireOp",EDGE,"E0.35"),sQuery(id+"F12.wireOp",EDGE,"E28")])],"isStart":false});
            extrude(context, id + "F14", {"entities" : qUnion([Q0, Q1, Q2, Q3, Q4, Q5]), "operationType" : NewBodyOperationType.ADD, "oppositeDirection" : true, "depth" : 148.08 * mm, "offsetDistance" : 25.4 * mm});
        }
        {
            var Q0;
            Q0=makeQuery(id+"F13.opExtrude","CAP_FACE",FACE,{"disambiguationData":[OSD([sQuery(id+"F0.wireOp",EDGE,"E0.34"),sQuery(id+"F0.wireOp",EDGE,"E0.35"),sQuery(id+"F12.wireOp",EDGE,"E23")])],"isStart":false});
            var Q1;
            Q1=makeQuery(id+"F13.opExtrude","CAP_FACE",FACE,{"disambiguationData":[OSD([sQuery(id+"F0.wireOp",EDGE,"E0.34"),sQuery(id+"F0.wireOp",EDGE,"E0.35"),sQuery(id+"F12.wireOp",EDGE,"E24")])],"isStart":false});
            var Q2;
            Q2=makeQuery(id+"F13.opExtrude","CAP_FACE",FACE,{"disambiguationData":[OSD([sQuery(id+"F0.wireOp",EDGE,"E0.34"),sQuery(id+"F0.wireOp",EDGE,"E0.35"),sQuery(id+"F12.wireOp",EDGE,"E25")])],"isStart":false});
            var Q3;
            Q3=makeQuery(id+"F13.opExtrude","CAP_FACE",FACE,{"disambiguationData":[OSD([sQuery(id+"F0.wireOp",EDGE,"E0.34"),sQuery(id+"F0.wireOp",EDGE,"E0.35"),sQuery(id+"F12.wireOp",EDGE,"E26")])],"isStart":false});
            var Q4;
            Q4=makeQuery(id+"F13.opExtrude","CAP_FACE",FACE,{"disambiguationData":[OSD([sQuery(id+"F0.wireOp",EDGE,"E0.34"),sQuery(id+"F0.wireOp",EDGE,"E0.35"),sQuery(id+"F12.wireOp",EDGE,"E27")])],"isStart":false});
            var Q5;
            Q5=makeQuery(id+"F13.opExtrude","CAP_FACE",FACE,{"disambiguationData":[OSD([sQuery(id+"F0.wireOp",EDGE,"E0.34"),sQuery(id+"F0.wireOp",EDGE,"E0.35"),sQuery(id+"F12.wireOp",EDGE,"E28")])],"isStart":false});
            extrude(context, id + "F15", {"entities" : qUnion([Q0, Q1, Q2, Q3, Q4, Q5]), "operationType" : NewBodyOperationType.ADD, "depth" : 120.4 * mm, "offsetDistance" : 25.4 * mm});
        }
    });
